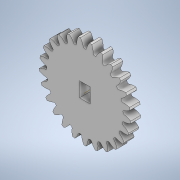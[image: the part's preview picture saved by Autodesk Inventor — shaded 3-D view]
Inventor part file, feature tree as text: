
AUTODESK INVENTOR PART (.ipt)
format: ipt  version: 2020 (Build 240168000, 168)  size: 312,320 bytes
history: native  units: mm
features: extrude x3, sketch x2, pattern_circular x1
ambient origin geometry x8: Origin, YZ Plane, XZ Plane, XY Plane, X Axis, Y Axis, Z Axis, Center Point
bodies: Solid1 (feature_tree)
feature tree (6):
  sketch  "Sketch1"  dims[d0=3.0mm d1=0.0mm d2=10.0mm d3=0.0mm]
  extrude  "Extrusion1"  Depth=10.0mm TaperAngle=0.0deg
  extrude  "Extrusion2"  Depth=3.2mm TaperAngle=0.0deg
  pattern_circular  "Circular Pattern1"  [2 undecoded]
  extrude  "Extrusion3"  Depth=3.2mm
  sketch  "Sketch2"  dims[d4=250.0mm d5=360.0deg d8=10.0mm d9=0.0mm d10=4.4mm d11=3.2mm]
note: 2 required parameter values undecoded (feature->parameter linkage not recoverable at this tier; creation-order binding heuristic only, values carry confidence <= 0.55)
